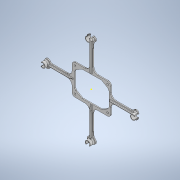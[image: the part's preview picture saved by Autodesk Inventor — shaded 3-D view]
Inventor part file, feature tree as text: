
AUTODESK INVENTOR PART (.ipt)
format: ipt  version: 2020 (Build 240168000, 168)  size: 1,679,360 bytes
history: native  units: in
note: dims shown in document units (in); Inventor stores cm internally (conversion verified against a paired STEP export)
features: sketch x13, extrude x12, fillet x7, chamfer x1
ambient origin geometry x8: Origin, YZ Plane, XZ Plane, XY Plane, X Axis, Y Axis, Z Axis, Center Point
bodies: Solid1 (feature_tree)
feature tree (33):
  extrude  "Extrusion1"  Depth=3.3071in
  extrude  "Extrusion2"  Depth=0.7874in
  extrude  "Extrusion4"  Depth=0.0787in TaperAngle=0.0deg
  extrude  "Extrusion5"  Depth=2.0079in
  fillet  "Fillet1"  Radius=0.1496in
  extrude  "Extrusion9"  Depth=0.1496in
  extrude  "Extrusion10"  Depth=0.2756in TaperAngle=0.0deg
  chamfer  "Chamfer3"  Distance=1.5748in Angle=360.0deg
  fillet  "Fillet3"  Radius=0.2756in
  extrude  "Extrusion11"  Depth=1.5748in TaperAngle=360.0deg
  extrude  "Extrusion12"  Depth=0.0787in
  fillet  "Fillet4"  Radius=0.3937in
  extrude  "Extrusion13"  Depth=0.1575in
  fillet  "Fillet5"  Radius=0.1496in
  fillet  "Fillet6"  Radius=1.5748in
  fillet  "Fillet7"  Radius=0.3937in
  fillet  "Fillet8"  Radius=0.1575in
  extrude  "Extrusion16"  Depth=0.3937in TaperAngle=360.0deg
  extrude  "Extrusion17"  Depth=0.3937in TaperAngle=0.0deg
  sketch  "Sketch21"  dims[d78=0.4724in d79=0.1496in d80=0.1496in d81=1.5748in d83=360.0deg d85=0.3937in d86=0.0in d89=0.1575in]
  extrude  "Extrusion18"  Depth=0.0787in TaperAngle=45.0deg
  sketch  "Sketch1"  dims[d0=3.3071in d1=3.3071in]
  sketch  "Sketch2"  dims[d2=4.2913in d3=0.7874in]
  sketch  "Sketch4"  dims[d4=1.5748in d6=360.0deg d8=0.0787in d9=0.0in]
  sketch  "Sketch5"  dims[d10=2.6772in d11=2.0079in d12=0.1496in]
  sketch  "Sketch9"  dims[d13=0.1496in d14=0.1496in]
  sketch  "Sketch11"  dims[d15=0.1496in d16=0.2756in d17=0.0in]
  sketch  "Sketch13"  dims[d24=0.1244in]
  sketch  "Sketch14"  dims[d25=0.1244in]
  sketch  "Sketch15"  dims[d26=0.1043in d27=1.5748in d29=360.0deg d31=0.2756in d32=0.0in]
  sketch  "Sketch19"  dims[d33=0.4224in d34=1.5748in d36=360.0deg]
  sketch  "Sketch20"  dims[d38=0.2953in d39=0.0in d40=0.0787in d77=0.3937in]
  sketch  "Sketch22"  dims[d90=0.0394in d91=1.5748in d93=360.0deg d95=0.1181in d96=0.0in d97=0.1181in d98=0.0787in d99=45.0deg d100=0.0394in d106=0.0394in d107=1.5748in d109=360.0deg d111=0.374in d112=0.0in d113=0.1181in d114=1.9685in d116=0.4724in d117=0.3937in d119=0.3937in d121=0.1181in d122=1.5748in d124=0.4724in d125=0.3937in d127=0.3937in d129=2.3622in d131=0.2756in d132=0.3937in d134=0.3937in d136=0.7874in d138=0.2756in d139=0.3937in d141=0.3937in d143=0.374in d144=0.0in d145=0.1969in d146=0.7874in d148=1.8898in d149=0.7874in d151=0.4724in d154=0.1575in d155=0.0984in d156=0.2362in d157=0.2362in d158=0.1575in d159=0.0984in d160=0.374in d161=0.0in d162=0.3937in d163=0.3937in d164=0.3937in d165=0.2362in d173=0.0787in d174=0.0787in d175=0.3543in d176=1.5748in d178=360.0deg d180=0.2362in d181=0.1575in d183=1.6929in d184=0.374in d185=0.0in d186=1.6929in d187=1.5354in d188=0.0787in d189=0.0in d190=0.3937in d191=0.0in d192=0.0984in]
